# Revit family: Faucet-Lavatory-KOHLER-Hint-K-97061
name_source: partatom
category: Plumbing Fixtures
revit_build: Autodesk Revit 2015 (Build: 20140606_1530(x64)
units: mm (PartAtom-declared; Revit-internal decimal feet)

## types (2) — shared parameters
ADA Compliant = Yes
Assembly Code = D2010
CW Connection = Yes
Cold Water Inlet = Cold Water Inlet
Date Modified = 03/13/2019
Default Elevation = 36"
Description = Single-handle bathroom sink faucet with escutcheon
Drain Included = Yes
Faucet Hole Spacing = 0"
Flow Rate = 1 GPM
HW Connection = Yes
Handle Clearance = 3 5/32"
Height = 6 1/2"
Hot Water Inlet = Hot Water Inlet
Length = 3 7/8"
Manufacturer = KOHLER Co.
MasterFormat 1995 = 15410
MasterFormat 2004 = 22.41.39
Material = Premium metal construction
Pressure = 60.00 psi
Product Documentation Link = https://www.us.kohler.com
Product Name = Hint
Product Page URL = http://www.us.kohler.com
Spout Reach = 3 7/8"
URL = https://www.us.kohler.com
Vent Connection = No
Waste Connection = No
Waste Water Outlet = Waste Water Outlet
WaterSense Certified = Yes
Width = 6 3/8"

## per-type parameters (varying)
| type | Finish | Model | Type |
| CP-Polished Chrome | Kohler-Metal-CP-Polished_Chrome | K-97061-4-CP | 1 |
| BN-Vibrant Brushed Nickel | Kohler-Metal-BN-Vibrant_Brushed_Nickel | K-97061-4-BN | 2 |

## geometry (parser evidence)
native form markers: Sweep x5
no freeform markers — native parametric forms only
